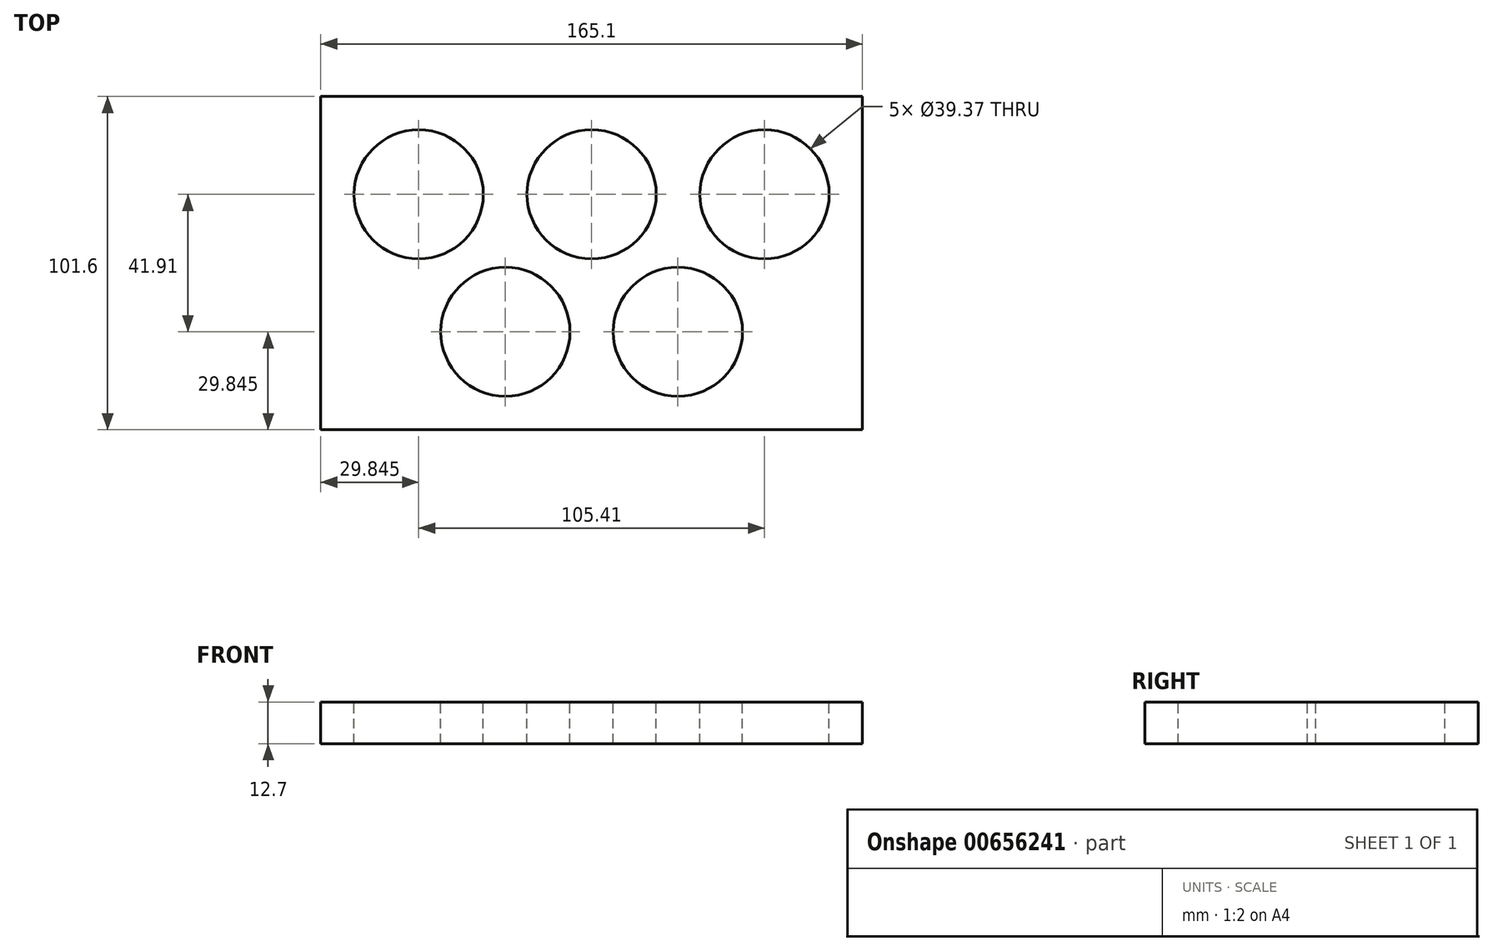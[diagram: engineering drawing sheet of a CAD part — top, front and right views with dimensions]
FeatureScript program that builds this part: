
annotation { "Feature Type Name" : "Feature", "Feature Type Description" : "" }
export const myFeature = defineFeature(function(context is Context, id is Id, definition is map)
    precondition{}
    {
        {
            var Q0;
            Q0=qCreatedBy(makeId("Top.planeOp"),FACE);
            var sketch = newSketch(context, id + "F0", { "sketchPlane" : qUnion([Q0])});
            skLineSegment(sketch, "E0.bottom", {"start": v(-82.55, -50.8) * mm, "end": v(82.55, -50.8) * mm});
            skLineSegment(sketch, "E0.top", {"start": v(-82.55, 50.8) * mm, "end": v(82.55, 50.8) * mm});
            skLineSegment(sketch, "E0.left", {"start": v(-82.55, -50.8) * mm, "end": v(-82.55, 50.8) * mm});
            skLineSegment(sketch, "E0.right", {"start": v(82.55, -50.8) * mm, "end": v(82.55, 50.8) * mm});
            skPoint(sketch, "E0.middle", {"position": v(0, 0) * mm});
            skCircle(sketch, "E1", {"center": v(-52.7, 20.95) * mm, "radius": 19.69 * mm});
            skCircle(sketch, "E2", {"center": v(0, 20.96) * mm, "radius": 19.69 * mm});
            skCircle(sketch, "E3", {"center": v(52.7, 20.96) * mm, "radius": 19.69 * mm});
            skCircle(sketch, "E4", {"center": v(-26.29, -20.96) * mm, "radius": 19.69 * mm});
            skCircle(sketch, "E5", {"center": v(26.29, -20.95) * mm, "radius": 19.69 * mm});
            skSolve(sketch);
        }
        {
            var Q0;
            Q0=makeQuery(id+"F0.imprint","IMPRINT",FACE,{"disambiguationData":[TD([[makeQuery(id+"F0.imprint","IMPRINT",EDGE,{"derivedFrom":sQuery(id+"F0.wireOp",EDGE,"E0.bottom")}),1.0]])]});
            extrude(context, id + "F1", {"entities" : qUnion([Q0]), "oppositeDirection" : true, "depth" : 12.7 * mm, "offsetDistance" : 25.4 * mm});
        }
    });
